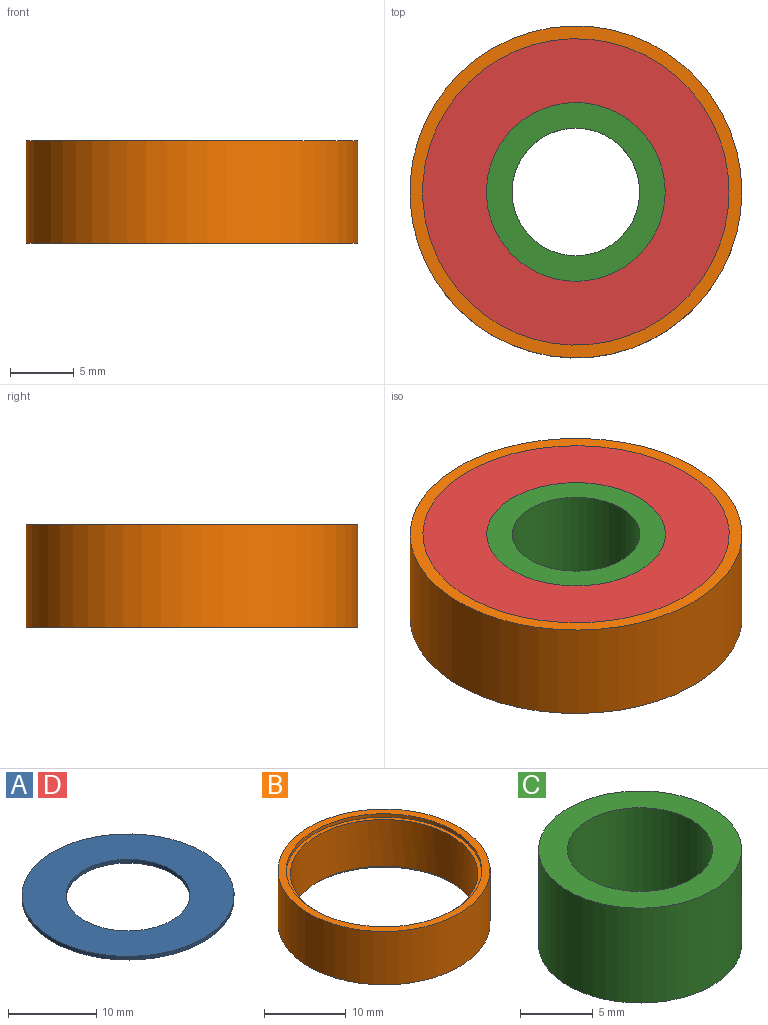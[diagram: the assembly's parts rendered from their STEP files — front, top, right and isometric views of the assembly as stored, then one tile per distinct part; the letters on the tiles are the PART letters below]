
ASSEMBLY  parts=4 mates=3
PART A: 4 faces, bbox 24x24x0.5 mm
  f0: cylinder r=7mm len=14mm, axis (0,0,-1), area 22mm2, adj f2,f3
  f1: cylinder r=12mm len=24mm, axis (0,0,-1), area 37.7mm2, adj f2,f3
  f2: plane 24x24mm, normal (0,0,1), area 298.5mm2, adj f0,f1
  f3: plane 24x24mm, normal (0,0,-1), area 298.5mm2, adj f0,f1
PART B: 8 faces, bbox 26x26x8 mm
  f0: cylinder r=11.5mm len=23mm, axis (0,0,-1), area 505.8mm2, adj f5,f7
  f1: cylinder r=13mm len=26mm, axis (0,0,-1), area 653.5mm2, adj f2,f3
  f2: plane 26x26mm, normal (0,0,1), area 78.5mm2, adj f1,f4
  f3: plane 26x26mm, normal (0,0,-1), area 78.5mm2, adj f1,f6
  f4: cylinder r=12mm len=24mm, axis (0,0,1), area 37.7mm2, adj f2,f5
  f5: plane 24x24mm, normal (0,0,1), area 36.9mm2, adj f0,f4
  f6: cylinder r=12mm len=24mm, axis (0,0,-1), area 37.7mm2, adj f3,f7
  f7: plane 24x24mm, normal (0,0,-1), area 36.9mm2, adj f0,f6
PART C: 4 faces, bbox 14x14x8 mm
  f0: cylinder r=5mm len=10mm, axis (0,0,-1), area 251.3mm2, adj f2,f3
  f1: cylinder r=7mm len=14mm, axis (0,0,-1), area 351.9mm2, adj f2,f3
  f2: plane 14x14mm, normal (0,0,1), area 75.4mm2, adj f0,f1
  f3: plane 14x14mm, normal (0,0,-1), area 75.4mm2, adj f0,f1
PART D: same geometry as A
PLACE A at identity
PLACE B at identity
PLACE C at identity
PLACE D t=(0,0,7.5)mm
MATE fastened A.f1 <-> B.f6  axis (0,0,1) through (0,0,0.5)mm
MATE revolute C.f1 <-> B.f4  axis (0,0,1) through (0,0,8)mm
MATE fastened D.f1 <-> B.f4  axis (0,0,-1) through (0,0,7.5)mm
